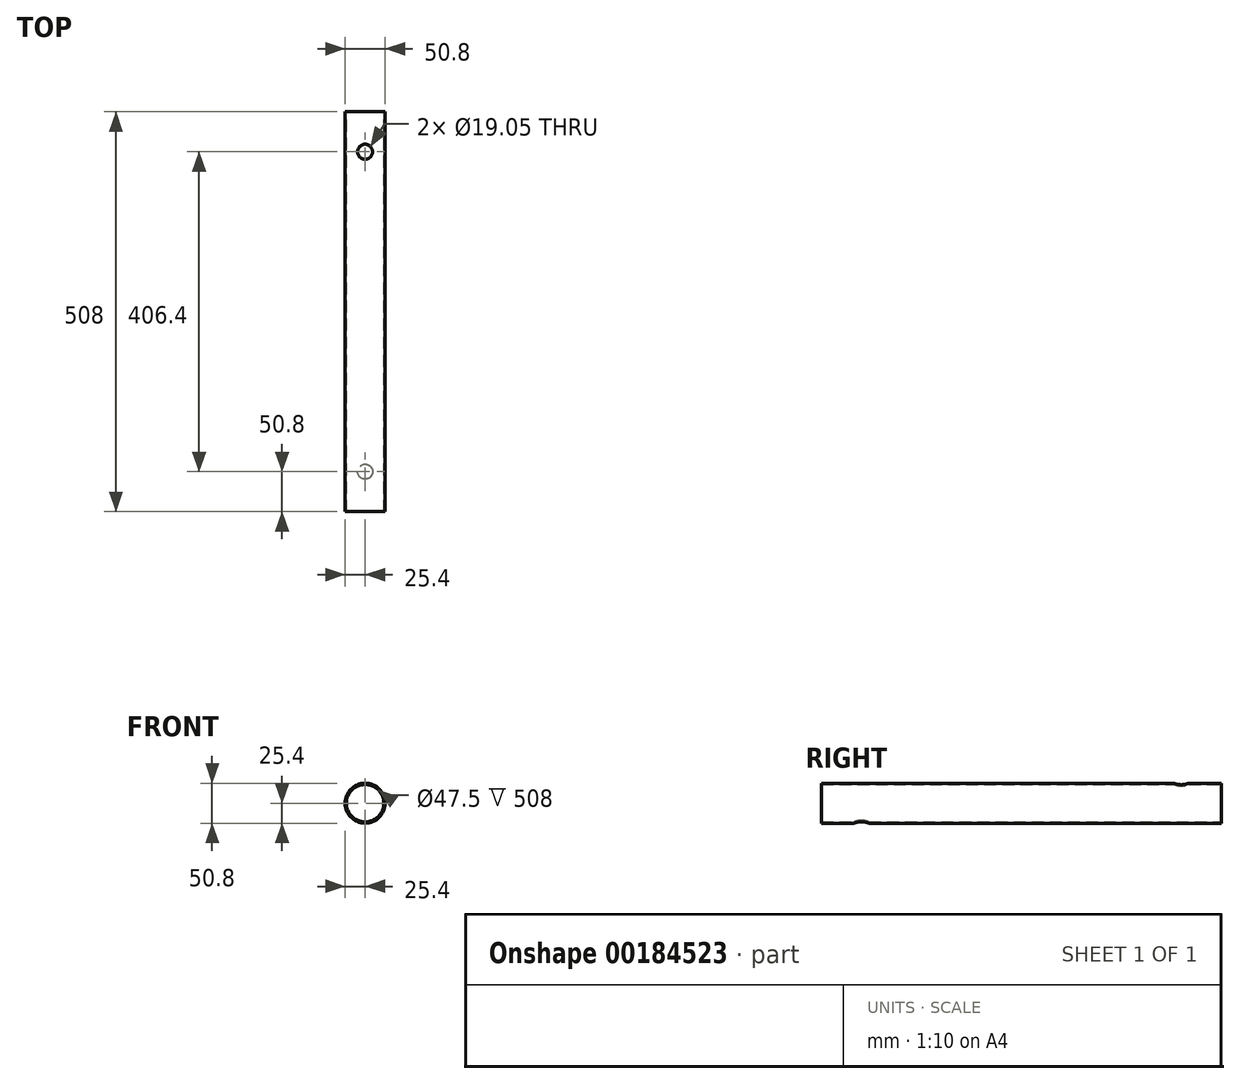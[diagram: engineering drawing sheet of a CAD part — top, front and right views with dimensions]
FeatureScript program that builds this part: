
annotation { "Feature Type Name" : "Feature", "Feature Type Description" : "" }
export const myFeature = defineFeature(function(context is Context, id is Id, definition is map)
    precondition{}
    {
        {
            var Q0;
            Q0=qCreatedBy(makeId("Front.planeOp"),FACE);
            var sketch = newSketch(context, id + "F0", { "sketchPlane" : qUnion([Q0])});
            skCircle(sketch, "E0", {"center": v(0, 0) * mm, "radius": 25.4 * mm});
            skCircle(sketch, "E1.0", {"center": v(0, 0) * mm, "radius": 23.75 * mm});
            skLineSegment(sketch, "E2", {"start": v(-11.94, 20.53) * mm, "end": v(-11.94, -20.53) * mm, "construction": true});
            skLineSegment(sketch, "E3", {"start": v(11.94, 20.53) * mm, "end": v(11.94, -20.53) * mm, "construction": true});
            skLineSegment(sketch, "E4", {"start": v(-20.53, 11.94) * mm, "end": v(20.53, 11.94) * mm, "construction": true});
            skLineSegment(sketch, "E5", {"start": v(-20.53, -11.94) * mm, "end": v(20.53, -11.94) * mm, "construction": true});
            skSolve(sketch);
        }
        {
            var Q0;
            Q0=makeQuery(id+"F0.imprint","IMPRINT",FACE,{"disambiguationData":[TD([[makeQuery(id+"F0.imprint","IMPRINT",EDGE,{"derivedFrom":sQuery(id+"F0.wireOp",EDGE,"E0")}),1.0]])]});
            extrude(context, id + "F1", {"entities" : qUnion([Q0]), "endBound" : BoundingType.SYMMETRIC, "depth" : 508 * mm});
        }
        {
            var Q0;
            Q0 = qSketchRegion(id + "F0", true);
            extrude(context, id + "F2", {"entities" : qUnion([Q0]), "operationType" : NewBodyOperationType.ADD, "endBound" : BoundingType.SYMMETRIC, "depth" : 508 * mm});
        }
        {
            var Q0;
            Q0=qCreatedBy(makeId("Top.planeOp"),FACE);
            var sketch = newSketch(context, id + "F3", { "sketchPlane" : qUnion([Q0])});
            skPoint(sketch, "E6", {"position": v(0, -203.2) * mm});
            skPoint(sketch, "E7", {"position": v(0, 598.57) * mm});
            skPoint(sketch, "E8", {"position": v(0, 203.2) * mm});
            skSolve(sketch);
        }
        {
            var Q0;
            Q0=sQuery(id+"F3.wireOp",VERTEX,"E8");
            var Q1;
            Q1=makeQuery(id+"F1.opExtrude","SWEPT_BODY",BODY,{"disambiguationData":[OSD([sQuery(id+"F0.wireOp",EDGE,"E0"),sQuery(id+"F0.wireOp",EDGE,"E1.0")])]});
            hole(context, id + "F4", {"style" : HoleStyle.SIMPLE, "endStyle" : HoleEndStyle.THROUGH, "oppositeDirection" : true, "holeDiameter" : 19.05 * mm, "locations" : qUnion([Q0]), "scope" : qUnion([Q1]), "isTappedThrough" : true});
        }
        {
            var Q0;
            Q0=sQuery(id+"F3.wireOp",VERTEX,"E6");
            var Q1;
            Q1=makeQuery(id+"F1.opExtrude","SWEPT_BODY",BODY,{"disambiguationData":[OSD([sQuery(id+"F0.wireOp",EDGE,"E0"),sQuery(id+"F0.wireOp",EDGE,"E1.0")])]});
            hole(context, id + "F5", {"style" : HoleStyle.SIMPLE, "endStyle" : HoleEndStyle.THROUGH, "holeDiameter" : 19.05 * mm, "locations" : qUnion([Q0]), "scope" : qUnion([Q1]), "isTappedThrough" : true});
        }
    });
